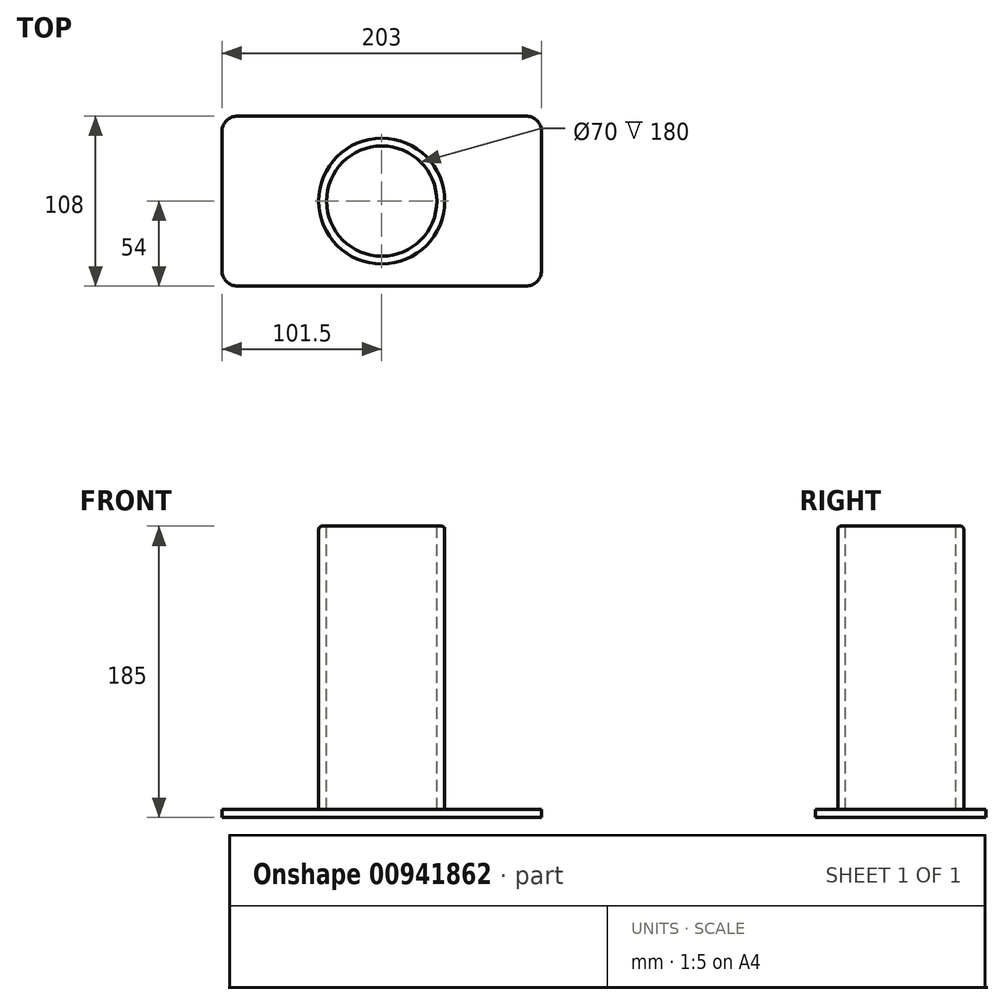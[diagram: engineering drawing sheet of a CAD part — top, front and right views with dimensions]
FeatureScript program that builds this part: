
annotation { "Feature Type Name" : "Feature", "Feature Type Description" : "" }
export const myFeature = defineFeature(function(context is Context, id is Id, definition is map)
    precondition{}
    {
        {
            var Q0;
            Q0=qCreatedBy(makeId("Top.planeOp"),FACE);
            var sketch = newSketch(context, id + "F0", { "sketchPlane" : qUnion([Q0])});
            skLineSegment(sketch, "E0.bottom", {"start": v(-101.5, 54) * mm, "end": v(101.5, 54) * mm});
            skLineSegment(sketch, "E0.top", {"start": v(-101.5, -54) * mm, "end": v(101.5, -54) * mm});
            skLineSegment(sketch, "E0.left", {"start": v(-101.5, 54) * mm, "end": v(-101.5, -54) * mm});
            skLineSegment(sketch, "E0.right", {"start": v(101.5, 54) * mm, "end": v(101.5, -54) * mm});
            skSolve(sketch);
        }
        {
            var Q0;
            Q0 = qSketchRegion(id + "F0", true);
            extrude(context, id + "F1", {"entities" : qUnion([Q0]), "depth" : 5 * mm, "offsetDistance" : 25 * mm});
        }
        {
            var Q0;
            Q0=makeQuery(id+"F1.opExtrude","CAP_FACE",FACE,{"disambiguationData":[OSD([sQuery(id+"F0.wireOp",EDGE,"E0.bottom"),sQuery(id+"F0.wireOp",EDGE,"E0.top"),sQuery(id+"F0.wireOp",EDGE,"E0.left"),sQuery(id+"F0.wireOp",EDGE,"E0.right")])],"isStart":false});
            var sketch = newSketch(context, id + "F2", { "sketchPlane" : qUnion([Q0])});
            skCircle(sketch, "E1", {"center": v(0, 0) * mm, "radius": 40 * mm});
            skSolve(sketch);
        }
        {
            var Q0;
            Q0 = qSketchRegion(id + "F2", true);
            extrude(context, id + "F3", {"entities" : qUnion([Q0]), "operationType" : NewBodyOperationType.ADD, "depth" : 180 * mm, "offsetDistance" : 25 * mm});
        }
        {
            var Q0;
            Q0=makeQuery(id+"F3.opExtrude","CAP_FACE",FACE,{"disambiguationData":[OSD([sQuery(id+"F2.wireOp",EDGE,"E1")])],"isStart":false});
            var sketch = newSketch(context, id + "F4", { "sketchPlane" : qUnion([Q0])});
            skCircle(sketch, "E2", {"center": v(0, 0) * mm, "radius": 35 * mm});
            skSolve(sketch);
        }
        {
            var Q0;
            Q0 = qSketchRegion(id + "F4", true);
            extrude(context, id + "F5", {"entities" : qUnion([Q0]), "operationType" : NewBodyOperationType.REMOVE, "oppositeDirection" : true, "depth" : 180 * mm, "offsetDistance" : 25 * mm});
        }
        {
            var Q0;
            Q0=makeQuery(id+"F1.opExtrude","SWEPT_EDGE",EDGE,{"disambiguationData":[OSD([sQuery(id+"F0.wireOp",EDGE,"E0.top"),sQuery(id+"F0.wireOp",EDGE,"E0.right")])]});
            var Q1;
            Q1=makeQuery(id+"F1.opExtrude","SWEPT_EDGE",EDGE,{"disambiguationData":[OSD([sQuery(id+"F0.wireOp",EDGE,"E0.bottom"),sQuery(id+"F0.wireOp",EDGE,"E0.right")])]});
            var Q2;
            Q2=makeQuery(id+"F1.opExtrude","SWEPT_EDGE",EDGE,{"disambiguationData":[OSD([sQuery(id+"F0.wireOp",EDGE,"E0.bottom"),sQuery(id+"F0.wireOp",EDGE,"E0.left")])]});
            var Q3;
            Q3=makeQuery(id+"F1.opExtrude","SWEPT_EDGE",EDGE,{"disambiguationData":[OSD([sQuery(id+"F0.wireOp",EDGE,"E0.top"),sQuery(id+"F0.wireOp",EDGE,"E0.left")])]});
            fillet(context, id + "F6", {"entities" : qUnion([Q0, Q1, Q2, Q3]), "radius" : 10 * mm, "tangentPropagation" : true, "allowEdgeOverflow" : false});
        }
        {
            var Q0;
            Q0=makeQuery(id+"F3.opExtrude","CAP_EDGE",EDGE,{"disambiguationData":[OSD([sQuery(id+"F2.wireOp",EDGE,"E1")])],"isStart":false});
            fillet(context, id + "F7", {"entities" : qUnion([Q0]), "radius" : 2 * mm, "tangentPropagation" : true, "allowEdgeOverflow" : false});
        }
    });
